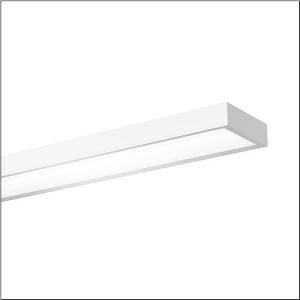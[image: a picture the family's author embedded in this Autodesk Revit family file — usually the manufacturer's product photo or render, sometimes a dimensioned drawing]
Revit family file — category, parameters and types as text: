
# Revit family: sport_31_51hs12dc3dca
name_source: partatom
category: Lighting Fixtures
units: mm (PartAtom-declared; Revit-internal decimal feet)

## family parameters
Cut with Voids When Loaded = No
Host = Face
Light Source = No
Part Type = Normal
Room Calculation Point = No
Round Connector Dimension = Use Diameter
Shared = No

## types (1)
- --- (1 x LED, 7500 lm, 55.4 W, 3000K)
    Apparent Load = 55 VA
    CIE Flux Codes = 65 89 97 100 100
    Color Rendering = 80
    Color Temperature = 3000K
    Default Elevation = 1800 mm
    Description = Sport 31, high bay luminaire, primary light control with reflector, of sheet steel, primary anti-glare with prismatic structure, of PC, primary optical cover: cover panel, of PC, light emission: direct distribution, primary light characteristic: symmetric, installation type: suspended mounting, recessed, surface-mounted, LED, rated luminous flux: 7.500lm, luminous efficacy: 130lm/W, light colour: 830, colour temperature: 3000K, control gear: DALI 2, with terminal, 5-pole, max. 2.5mm², mains connection: 220..240V, AC/DC, 50/60Hz, rated input power: 58W, housing, of sheet steel, traffic white (RAL 9016), length: 1.540mm, width: 315mm, height: 95mm, protection rating (complete): IP20, protection rating (lamp compartment, on room side): IP50, insulation class (complete): insulation class I (protective earthing), certification: CE, ENEC, UKCA, ball protection: ball impact resistant with ceiling mounting or chain suspension, impact resistance: IK08, permissible operating ambient temperature: -20..+35°C, standard: DIN 18032-3, EN 60598-2-22, packaging unit: 1 piece
    Height = 100 mm  [stored 0.328084 ft]
    Lamp = 1 x LED
    Lamp Light Flux = 7500 lm
    Lamp Power = 55.4 W
    Lamp count = 1
    Length = 1500 mm
    Luminous efficacy = 135 lm/W
    Manufacturer = Siteco
    ModVariant = No
    Model = 51HS12DC3DCA
    Mounting Place = Ceiling
    Mounting Type = Pendant
    Number of Poles = 1
    OnlyDefault = Yes
    Power Factor = 1
    Product Name = Sport 31
    Product group = high bay luminaire
    ProductGroupID = 902
    Protection Class = Protection class I
    Protection Degree = IP 20
    RLX_Detail_Level = 1
    RLX_Emergency_Light_Flux = 0 lm
    RLX_Emergency_Type = 0
    RLX_Emergency_Type_DB = No
    RlxData = <blob elided: 22765 chars, md5=ca2a77f0>
    Socket = socket
    Standby Power = 0 W
    System Light Flux = 7500 lm
    System Power = 55 W
    Type Comments = factory setting: luminous flux: 100 % | dim-lin: 254 | 234 mA
    Type Image = l_1397489.jpg
    URL = http://relux.com
    VarID = @adj_196289
    Voltage = 0 V
    Weight = 0.00 kg
    Width = 315 mm

note: [stored X ft] marks values corroborated as IEEE doubles in the binary element streams (Revit-internal decimal feet)

## geometry (parser evidence)
native form markers: Blend x4, Sweep x12
no freeform markers — native parametric forms only
